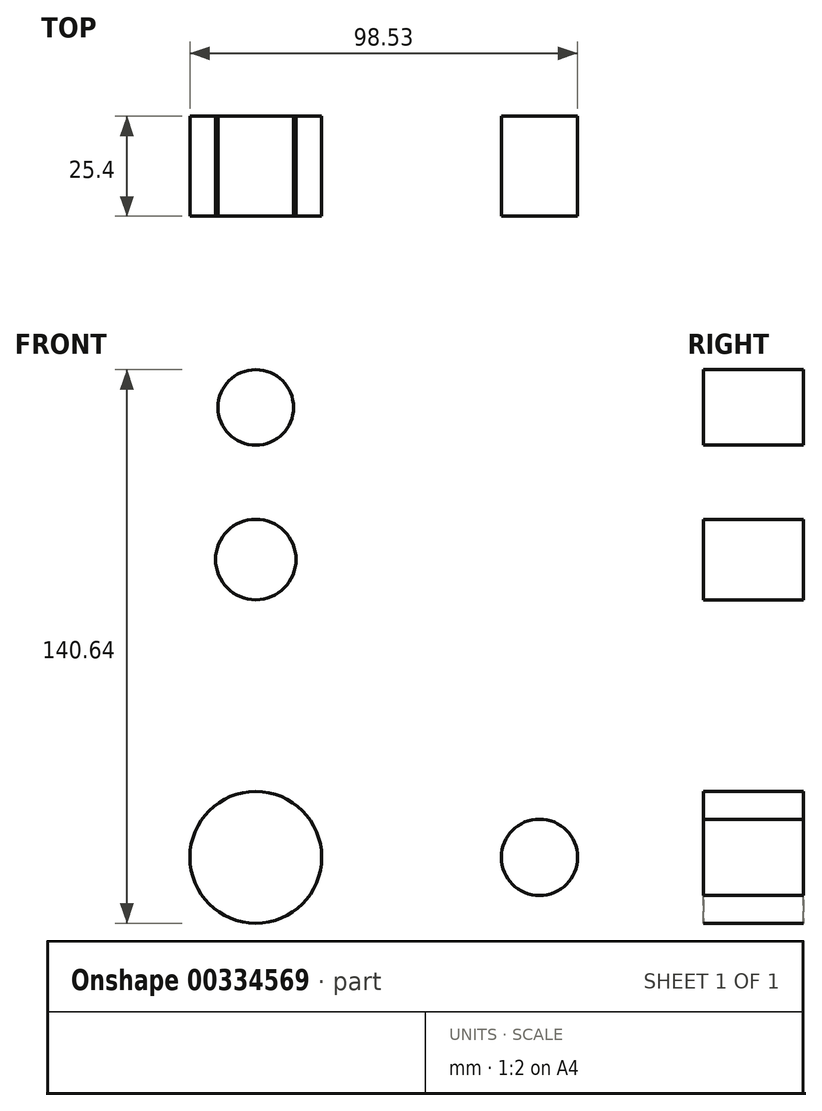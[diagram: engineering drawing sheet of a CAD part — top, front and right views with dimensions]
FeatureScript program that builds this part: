
annotation { "Feature Type Name" : "Feature", "Feature Type Description" : "" }
export const myFeature = defineFeature(function(context is Context, id is Id, definition is map)
    precondition{}
    {
        {
            var Q0;
            Q0=qCreatedBy(makeId("Front.planeOp"),FACE);
            var sketch = newSketch(context, id + "F0", { "sketchPlane" : qUnion([Q0])});
            skLineSegment(sketch, "E0", {"start": v(0, 0) * mm, "end": v(0, 114.3) * mm});
            skLineSegment(sketch, "E1", {"start": v(0, 0) * mm, "end": v(72.08, 0) * mm});
            skCircle(sketch, "E2", {"center": v(0, 114.3) * mm, "radius": 9.6 * mm});
            skCircle(sketch, "E3", {"center": v(0, 75.68) * mm, "radius": 10.22 * mm});
            skCircle(sketch, "E4", {"center": v(0, 0) * mm, "radius": 16.75 * mm});
            skCircle(sketch, "E5", {"center": v(72.08, 0) * mm, "radius": 9.7 * mm});
            skSolve(sketch);
        }
        {
            var Q0;
            Q0 = qSketchRegion(id + "F0", true);
            extrude(context, id + "F1", {"entities" : qUnion([Q0]), "depth" : 25.4 * mm});
        }
    });
